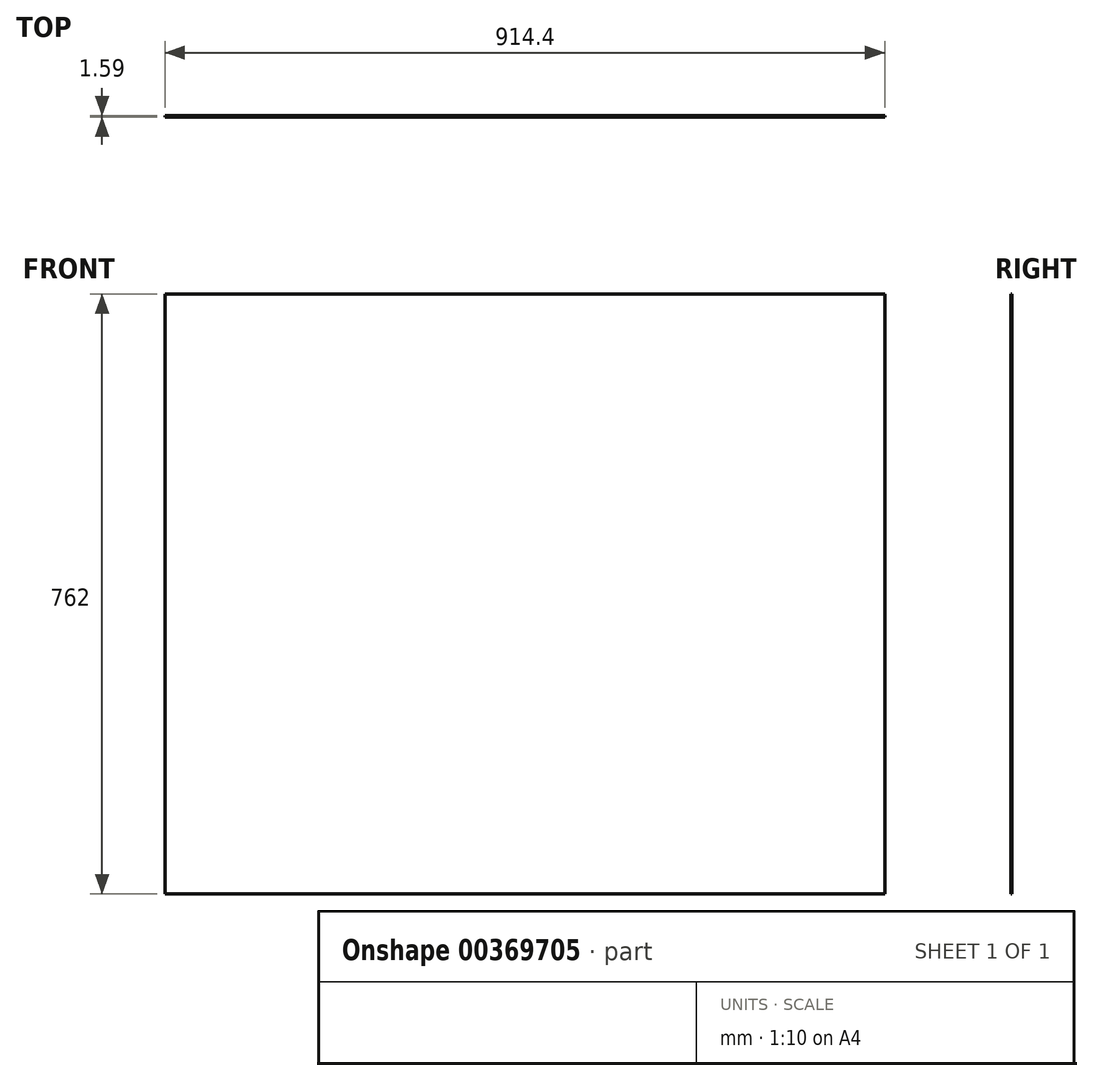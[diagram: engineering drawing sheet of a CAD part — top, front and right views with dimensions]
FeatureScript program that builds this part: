
annotation { "Feature Type Name" : "Feature", "Feature Type Description" : "" }
export const myFeature = defineFeature(function(context is Context, id is Id, definition is map)
    precondition{}
    {
        {
            var Q0;
            Q0=qCreatedBy(makeId("Front.planeOp"),FACE);
            var sketch = newSketch(context, id + "F0", { "sketchPlane" : qUnion([Q0])});
            skPoint(sketch, "E0.middle", {"position": v(0, 0) * mm});
            skLineSegment(sketch, "E1.bottom", {"start": v(457.2, -381) * mm, "end": v(-457.2, -381) * mm});
            skLineSegment(sketch, "E1.top", {"start": v(457.2, 381) * mm, "end": v(-457.2, 381) * mm});
            skLineSegment(sketch, "E1.left", {"start": v(457.2, -381) * mm, "end": v(457.2, 381) * mm});
            skLineSegment(sketch, "E1.right", {"start": v(-457.2, -381) * mm, "end": v(-457.2, 381) * mm});
            skSolve(sketch);
        }
        {
            var Q0;
            Q0=makeQuery(id+"F0.imprint","IMPRINT",FACE,{"disambiguationData":[TD([[makeQuery(id+"F0.imprint","IMPRINT",EDGE,{"derivedFrom":sQuery(id+"F0.wireOp",EDGE,"E1.bottom")}),-1.0]])]});
            extrude(context, id + "F1", {"entities" : qUnion([Q0]), "depth" : -1.59 * mm});
        }
    });
